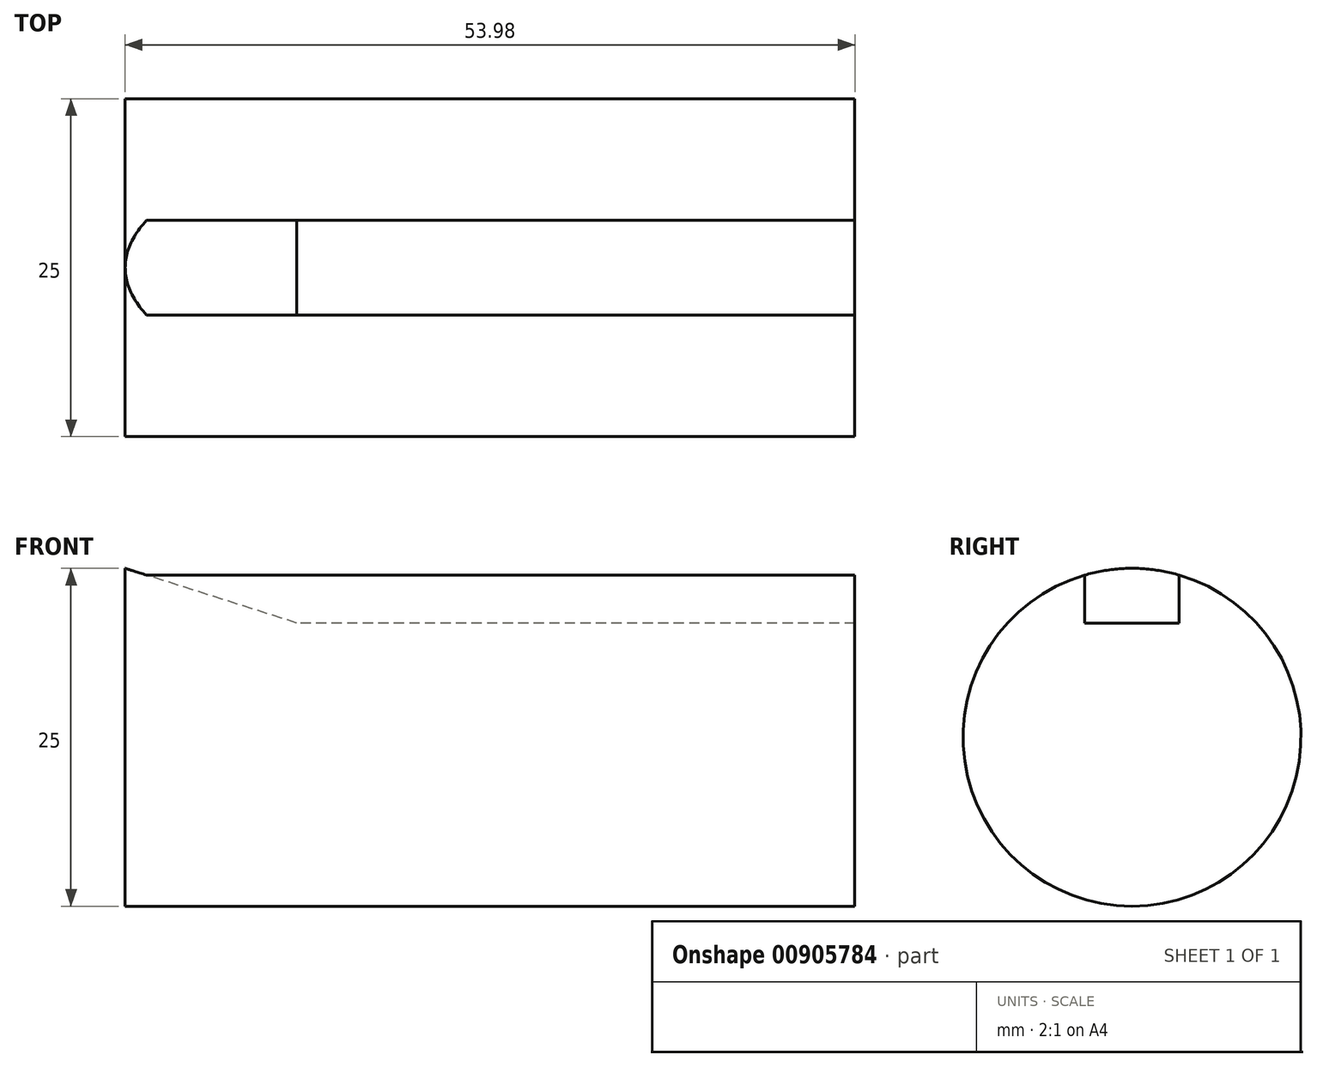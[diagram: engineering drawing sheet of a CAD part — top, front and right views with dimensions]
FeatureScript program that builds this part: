
annotation { "Feature Type Name" : "Feature", "Feature Type Description" : "" }
export const myFeature = defineFeature(function(context is Context, id is Id, definition is map)
    precondition{}
    {
        {
            var Q0;
            Q0=qCreatedBy(makeId("Right.planeOp"),FACE);
            var sketch = newSketch(context, id + "F0", { "sketchPlane" : qUnion([Q0])});
            skCircle(sketch, "E0", {"center": v(0, 0) * mm, "radius": 12.5 * mm});
            skSolve(sketch);
        }
        {
            var Q0;
            Q0 = qSketchRegion(id + "F0", true);
            extrude(context, id + "F1", {"entities" : qUnion([Q0]), "depth" : 53.97 * mm, "offsetDistance" : 25.4 * mm});
        }
        {
            var Q0;
            Q0=qCreatedBy(makeId("Right.planeOp"),FACE);
            cPlane(context, id + "F2", {"entities" : qUnion([Q0]), "cplaneType" : CPlaneType.OFFSET, "offset" : 12.7 * mm, "width" : 152.4 * mm, "height" : 152.4 * mm});
        }
        {
            var Q0;
            Q0=qCreatedBy(id+"F2.planeOp",FACE);
            var sketch = newSketch(context, id + "F3", { "sketchPlane" : qUnion([Q0])});
            skLineSegment(sketch, "E1.bottom", {"start": v(-3.5, 12.5) * mm, "end": v(3.5, 12.5) * mm});
            skLineSegment(sketch, "E1.top", {"start": v(-3.5, 8.45) * mm, "end": v(3.5, 8.45) * mm});
            skLineSegment(sketch, "E1.left", {"start": v(-3.5, 12.5) * mm, "end": v(-3.5, 8.45) * mm});
            skLineSegment(sketch, "E1.right", {"start": v(3.5, 12.5) * mm, "end": v(3.5, 8.45) * mm});
            skPoint(sketch, "E2", {"position": v(0, -12.5) * mm});
            skSolve(sketch);
        }
        {
            var Q0;
            Q0 = qSketchRegion(id + "F3", true);
            extrude(context, id + "F4", {"entities" : qUnion([Q0]), "operationType" : NewBodyOperationType.REMOVE, "endBound" : BoundingType.THROUGH_ALL, "depth" : 76.75 * mm, "offsetDistance" : 25.4 * mm});
        }
        {
            var Q0;
            Q0=qCreatedBy(makeId("Front.planeOp"),FACE);
            var sketch = newSketch(context, id + "F5", { "sketchPlane" : qUnion([Q0])});
            skLineSegment(sketch, "E3", {"start": v(12.7, 8.46) * mm, "end": v(0, 12.5) * mm});
            skLineSegment(sketch, "E4", {"start": v(0, 12.5) * mm, "end": v(12.7, 12.5) * mm});
            skLineSegment(sketch, "E5", {"start": v(12.7, 8.45) * mm, "end": v(12.7, 12.5) * mm});
            skPoint(sketch, "E6.0.2.end.orphan", {"position": v(53.98, 8.45) * mm});
            skPoint(sketch, "E6.0.2.start.orphan", {"position": v(12.7, 8.45) * mm});
            skPoint(sketch, "E6.0.0.start.orphan", {"position": v(53.98, 8.45) * mm});
            skSolve(sketch);
        }
        {
            var Q0;
            Q0 = qSketchRegion(id + "F5", true);
            extrude(context, id + "F6", {"entities" : qUnion([Q0]), "operationType" : NewBodyOperationType.REMOVE, "endBound" : BoundingType.SYMMETRIC, "oppositeDirection" : true, "depth" : 7 * mm, "offsetDistance" : 25.4 * mm});
        }
    });
